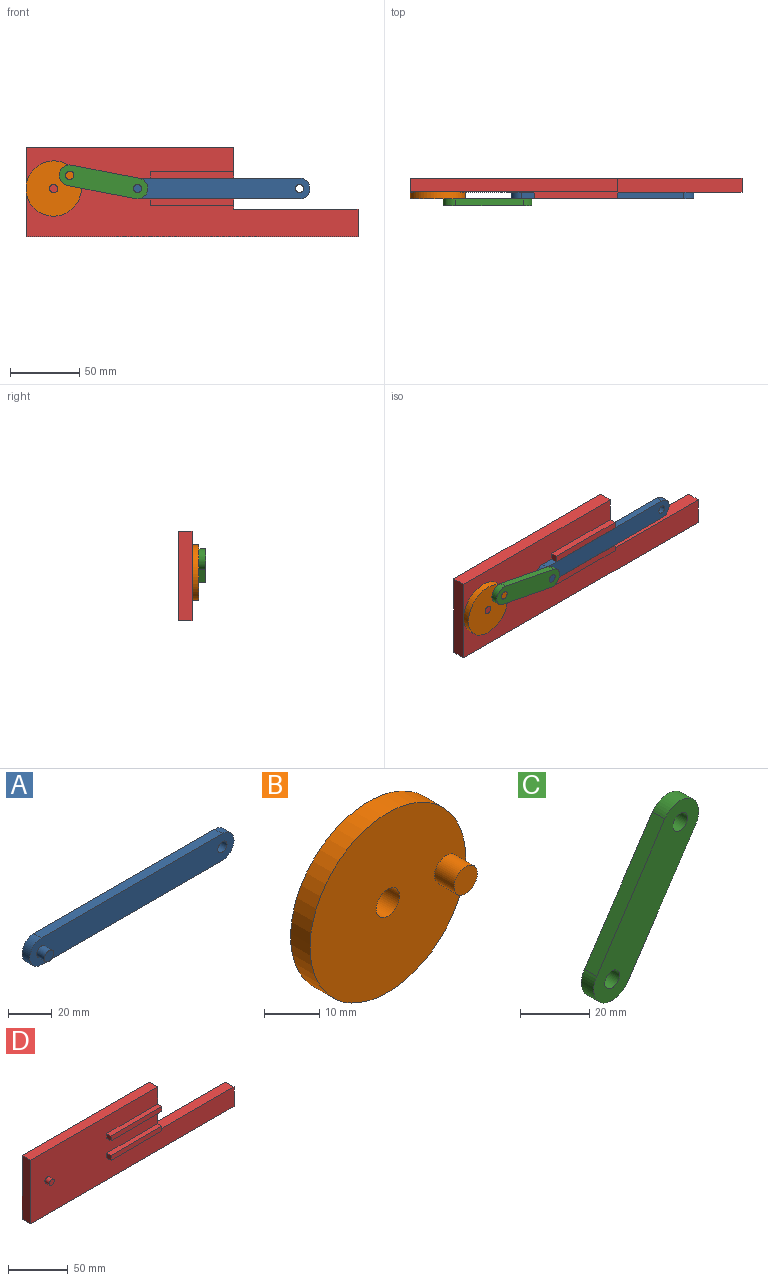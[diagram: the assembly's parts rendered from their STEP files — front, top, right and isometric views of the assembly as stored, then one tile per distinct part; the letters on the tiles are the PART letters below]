
ASSEMBLY  parts=4 mates=7
PART A: 9 faces, bbox 132.1x10x15 mm
  f0: plane 117.11x5mm, normal (0,0,1), area 585.5mm2, adj f1,f4,f5,f6
  f1: cylinder r=7.5mm len=15mm, axis (0,1,0), area 117.8mm2, adj f0,f2,f5,f6
  f2: plane 117.11x5mm, normal (0,0,-1), area 585.5mm2, adj f1,f4,f5,f6
  f3: cylinder r=3mm len=6mm, axis (0,1,0), area 94.2mm2, adj f5,f6
  f4: cylinder r=7.5mm len=15mm, axis (0,1,0), area 117.8mm2, adj f0,f2,f5,f6
  f5: plane 132.11x15mm, normal (0,-1,0), area 1876.7mm2, adj f0,f1,f2,f3,f4,f7
  f6: plane 132.11x15mm, normal (0,1,0), area 1905mm2, adj f0,f1,f2,f3,f4
  f7: cylinder r=3mm len=6mm, axis (0,1,0), area 94.2mm2, adj f5,f8
  f8: plane 6x6mm, normal (0,-1,0), area 28.3mm2, adj f7
PART B: 6 faces, bbox 40x10x40 mm
  f0: cylinder r=3mm len=6mm, axis (0,1,0), area 94.2mm2, adj f2,f3
  f1: cylinder r=20mm len=40mm, axis (0,1,0), area 628.3mm2, adj f2,f3
  f2: plane 40x40mm, normal (0,-1,0), area 1200.1mm2, adj f0,f1,f4
  f3: plane 40x40mm, normal (0,1,0), area 1228.4mm2, adj f0,f1
  f4: cylinder r=3mm len=6mm, axis (0,1,0), area 94.2mm2, adj f2,f5
  f5: plane 6x6mm, normal (0,-1,0), area 28.3mm2, adj f4
PART C: 8 faces, bbox 42.7x5x56.6 mm
  f0: plane 41.61x27.72mm, normal (-0.83,0,0.55), area 250mm2, adj f1,f4,f6,f7
  f1: cylinder r=7.5mm len=13.74mm, axis (0,1,0), area 117.8mm2, adj f0,f2,f6,f7
  f2: plane 41.61x27.72mm, normal (0.83,0,-0.55), area 250mm2, adj f1,f4,f6,f7
  f3: cylinder r=3mm len=6mm, axis (0,1,0), area 94.2mm2, adj f6,f7
  f4: cylinder r=7.5mm len=13.74mm, axis (0,1,0), area 117.8mm2, adj f0,f2,f6,f7
  f5: cylinder r=3mm len=6mm, axis (0,1,0), area 94.2mm2, adj f6,f7
  f6: plane 56.61x42.72mm, normal (0,-1,0), area 870.2mm2, adj f0,f1,f2,f3,f4,f5
  f7: plane 56.61x42.72mm, normal (0,1,0), area 870.2mm2, adj f0,f1,f2,f3,f4,f5
PART D: 18 faces, bbox 240x15x65 mm
  f0: plane 45x15mm, normal (1,0,0), area 500mm2, adj f1,f4,f5,f6,f8,f9,f10,f12
  f1: plane 240x65mm, normal (0,-1,0), area 10921.7mm2, adj f0,f2,f3,f4,f6,f7,f8,f10
  f2: plane 65x10mm, normal (-1,0,0), area 650mm2, adj f1,f3,f4,f5
  f3: plane 240x10mm, normal (0,0,-1), area 2400mm2, adj f1,f2,f5,f17
  f4: plane 150x10mm, normal (0,0,1), area 1500mm2, adj f0,f1,f2,f5
  f5: plane 240x65mm, normal (0,1,0), area 11550mm2, adj f0,f2,f3,f4,f16,f17
  f6: plane 60x5mm, normal (0,0,1), area 300mm2, adj f0,f1,f7,f9
  f7: plane 5x5mm, normal (-1,0,0), area 25mm2, adj f1,f6,f8,f9
  f8: plane 60x5mm, normal (0,0,-1), area 300mm2, adj f0,f1,f7,f9
  f9: plane 60x5mm, normal (0,-1,0), area 300mm2, adj f0,f6,f7,f8
  f10: plane 60x5mm, normal (0,0,1), area 300mm2, adj f0,f1,f11,f13
  f11: plane 5x5mm, normal (-1,0,0), area 25mm2, adj f1,f10,f12,f13
  f12: plane 60x5mm, normal (0,0,-1), area 300mm2, adj f0,f1,f11,f13
  f13: plane 60x5mm, normal (0,-1,0), area 300mm2, adj f0,f10,f11,f12
  f14: cylinder r=3mm len=6mm, axis (0,1,0), area 94.2mm2, adj f1,f15
  f15: plane 6x6mm, normal (0,-1,0), area 28.3mm2, adj f14
  f16: plane 90x10mm, normal (0,0,1), area 900mm2, adj f0,f1,f5,f17
  f17: plane 20x10mm, normal (1,0,0), area 200mm2, adj f1,f3,f5,f16
PLACE A t=(28.53,0,35)mm
PLACE B rot(axis=(0,-1,0),39.5deg) t=(8.96,0,116.37)mm
PLACE C rot(axis=(0,-1,0),112.7deg) t=(100.66,-5,35)mm
PLACE D t=(40,0,35)mm fixed
MATE cylindrical C.f3 <-> A.f1  axis (0,1,0) through (100.66,-5,35)mm
MATE planar B.f0 <-> D.f14  axis (0,1,0) through (40,0,35)mm
MATE revolute B.f0 <-> D.f14  axis (0,1,0) through (40,0,35)mm
MATE revolute B.f4 <-> C.f4  axis (0,-1,0) through (51.58,-5,44.54)mm
MATE planar A.f5 <-> C.f7  axis (0,-1,0) through (159.21,-5,35)mm
MATE planar A.f0 <-> D.f12  axis (0,0,1) through (159.21,-2.5,42.5)mm
MATE planar A.f6 <-> D.f1  axis (0,1,0) through (158.34,0,35)mm
